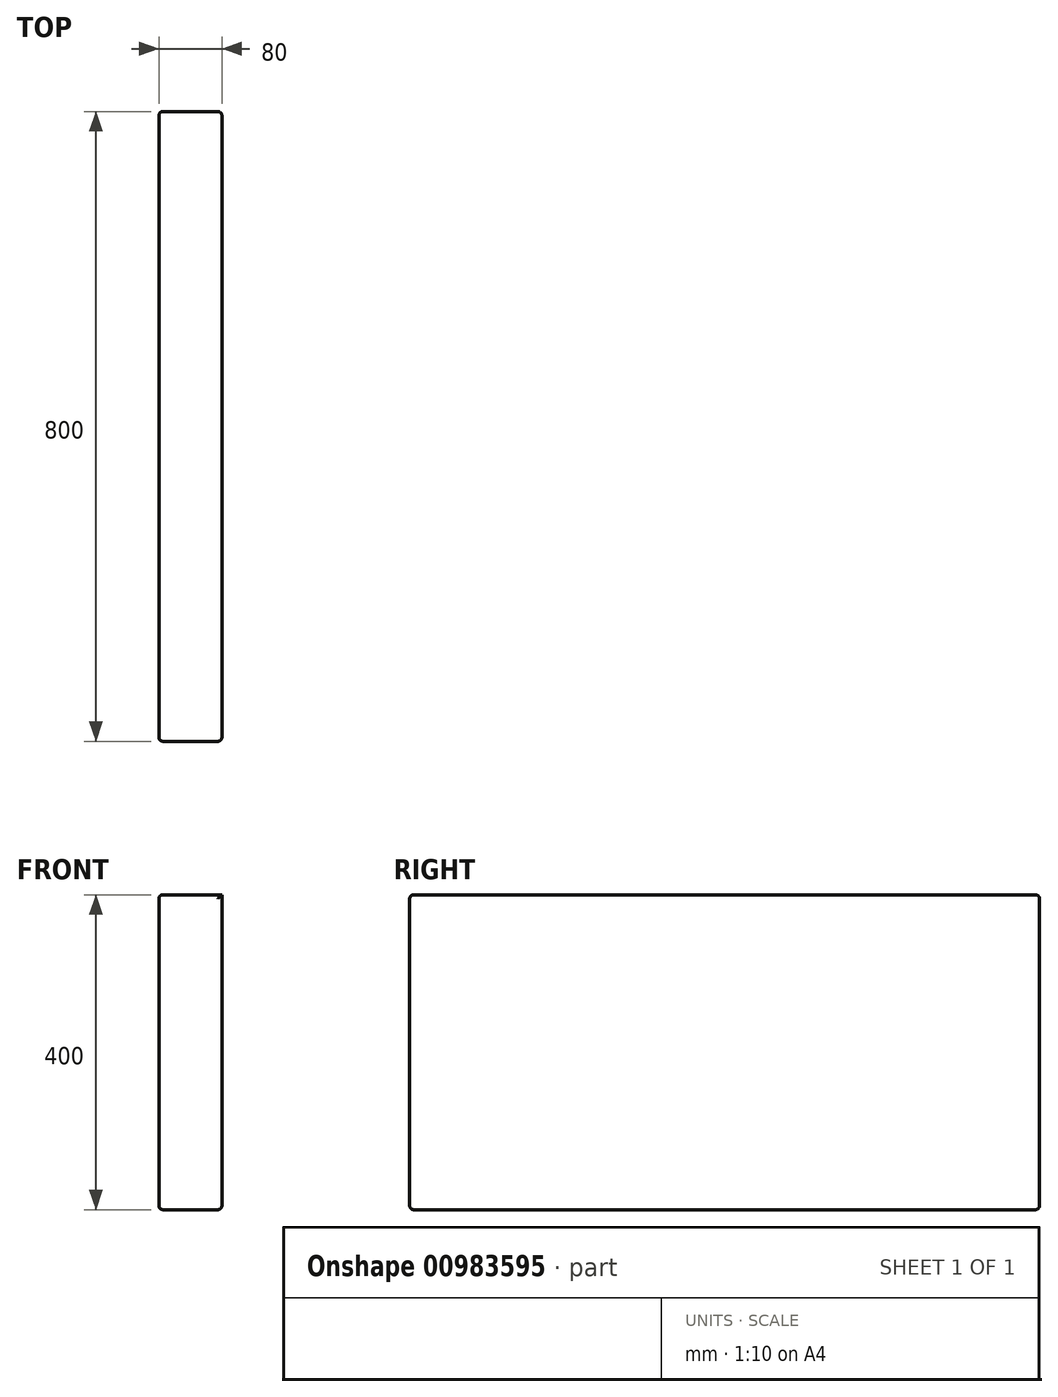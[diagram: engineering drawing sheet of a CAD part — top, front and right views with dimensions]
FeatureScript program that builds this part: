
annotation { "Feature Type Name" : "Feature", "Feature Type Description" : "" }
export const myFeature = defineFeature(function(context is Context, id is Id, definition is map)
    precondition{}
    {
        {
            var Q0;
            Q0=qCreatedBy(makeId("Right.planeOp"),FACE);
            var sketch = newSketch(context, id + "F0", { "sketchPlane" : qUnion([Q0])});
            skLineSegment(sketch, "E0.bottom", {"start": v(400, -200) * mm, "end": v(-400, -200) * mm});
            skLineSegment(sketch, "E0.top", {"start": v(400, 200) * mm, "end": v(-400, 200) * mm});
            skLineSegment(sketch, "E0.left", {"start": v(400, -200) * mm, "end": v(400, 200) * mm});
            skLineSegment(sketch, "E0.right", {"start": v(-400, -200) * mm, "end": v(-400, 200) * mm});
            skPoint(sketch, "E0.middle", {"position": v(0, 0) * mm});
            skSolve(sketch);
        }
        {
            var Q0;
            Q0=makeQuery(id+"F0.imprint","IMPRINT",FACE,{"disambiguationData":[TD([[makeQuery(id+"F0.imprint","IMPRINT",EDGE,{"derivedFrom":sQuery(id+"F0.wireOp",EDGE,"E0.bottom")}),-1.0]])]});
            extrude(context, id + "F1", {"entities" : qUnion([Q0]), "oppositeDirection" : true, "depth" : 80 * mm, "offsetDistance" : 25 * mm});
        }
        {
            var Q0;
            Q0=makeQuery(id+"F1.opExtrude","CAP_EDGE",EDGE,{"disambiguationData":[OSD([sQuery(id+"F0.wireOp",EDGE,"E0.top")])],"isStart":false});
            var Q1;
            Q1=makeQuery(id+"F1.opExtrude","CAP_EDGE",EDGE,{"disambiguationData":[OSD([sQuery(id+"F0.wireOp",EDGE,"E0.right")])],"isStart":false});
            var Q2;
            Q2=makeQuery(id+"F1.opExtrude","CAP_EDGE",EDGE,{"disambiguationData":[OSD([sQuery(id+"F0.wireOp",EDGE,"E0.right")])],"isStart":true});
            var Q3;
            Q3=makeQuery(id+"F1.opExtrude","CAP_EDGE",EDGE,{"disambiguationData":[OSD([sQuery(id+"F0.wireOp",EDGE,"E0.bottom")])],"isStart":true});
            var Q4;
            Q4=makeQuery(id+"F1.opExtrude","CAP_EDGE",EDGE,{"disambiguationData":[OSD([sQuery(id+"F0.wireOp",EDGE,"E0.bottom")])],"isStart":false});
            var Q5;
            Q5=makeQuery(id+"F1.opExtrude","CAP_EDGE",EDGE,{"disambiguationData":[OSD([sQuery(id+"F0.wireOp",EDGE,"E0.left")])],"isStart":false});
            var Q6;
            Q6=makeQuery(id+"F1.opExtrude","CAP_EDGE",EDGE,{"disambiguationData":[OSD([sQuery(id+"F0.wireOp",EDGE,"E0.left")])],"isStart":true});
            var Q7;
            Q7=makeQuery(id+"F1.opExtrude","SWEPT_EDGE",EDGE,{"disambiguationData":[OSD([sQuery(id+"F0.wireOp",EDGE,"E0.top"),sQuery(id+"F0.wireOp",EDGE,"E0.left")])]});
            var Q8;
            Q8=makeQuery(id+"F1.opExtrude","SWEPT_EDGE",EDGE,{"disambiguationData":[OSD([sQuery(id+"F0.wireOp",EDGE,"E0.bottom"),sQuery(id+"F0.wireOp",EDGE,"E0.left")])]});
            var Q9;
            Q9=makeQuery(id+"F1.opExtrude","SWEPT_EDGE",EDGE,{"disambiguationData":[OSD([sQuery(id+"F0.wireOp",EDGE,"E0.top"),sQuery(id+"F0.wireOp",EDGE,"E0.right")])]});
            var Q10;
            Q10=makeQuery(id+"F1.opExtrude","SWEPT_EDGE",EDGE,{"disambiguationData":[OSD([sQuery(id+"F0.wireOp",EDGE,"E0.bottom"),sQuery(id+"F0.wireOp",EDGE,"E0.right")])]});
            fillet(context, id + "F2", {"entities" : qUnion([Q0, Q1, Q2, Q3, Q4, Q5, Q6, Q7, Q8, Q9, Q10]), "tangentPropagation" : true, "radius" : 5 * mm, "defaultsChanged" : false, "vertexSettings" : [], "allowEdgeOverflow" : false});
        }
    });
